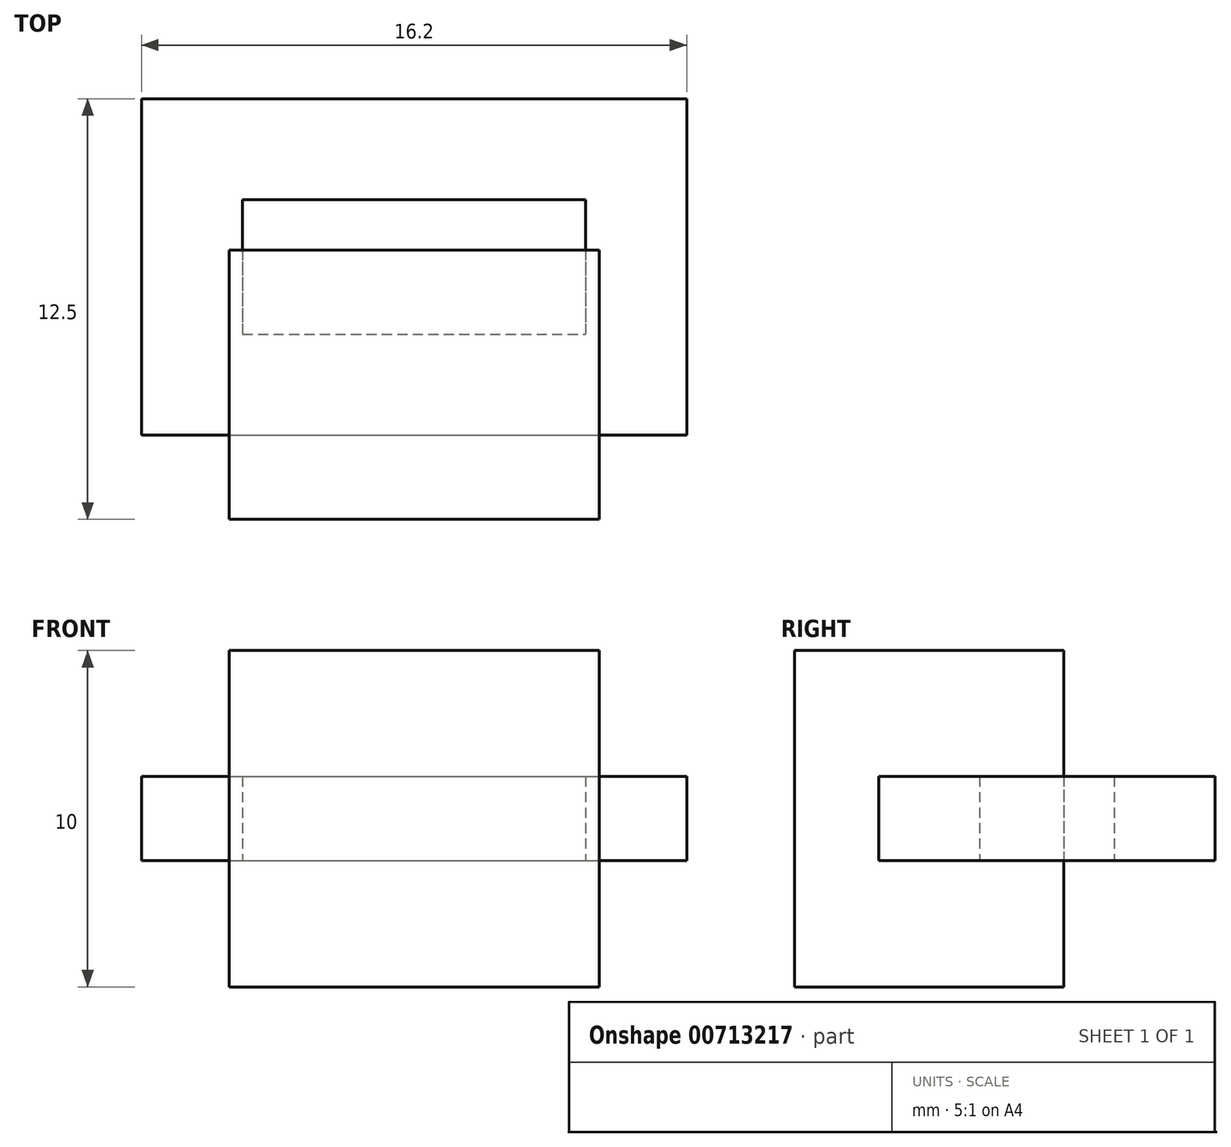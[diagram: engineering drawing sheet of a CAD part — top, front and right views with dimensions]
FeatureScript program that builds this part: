
annotation { "Feature Type Name" : "Feature", "Feature Type Description" : "" }
export const myFeature = defineFeature(function(context is Context, id is Id, definition is map)
    precondition{}
    {
        {
            var Q0;
            Q0=qCreatedBy(makeId("Top.planeOp"),FACE);
            var sketch = newSketch(context, id + "F0", { "sketchPlane" : qUnion([Q0])});
            skLineSegment(sketch, "E0.bottom", {"start": v(-8.1, -2) * mm, "end": v(8.1, -2) * mm});
            skLineSegment(sketch, "E0.top", {"start": v(-8.1, -12) * mm, "end": v(8.1, -12) * mm});
            skLineSegment(sketch, "E0.left", {"start": v(-8.1, -2) * mm, "end": v(-8.1, -12) * mm});
            skLineSegment(sketch, "E0.right", {"start": v(8.1, -2) * mm, "end": v(8.1, -12) * mm});
            skLineSegment(sketch, "E1.bottom", {"start": v(-5.1, -5) * mm, "end": v(5.1, -5) * mm});
            skLineSegment(sketch, "E1.top", {"start": v(-5.1, -9) * mm, "end": v(5.1, -9) * mm});
            skLineSegment(sketch, "E1.left", {"start": v(-5.1, -5) * mm, "end": v(-5.1, -9) * mm});
            skLineSegment(sketch, "E1.right", {"start": v(5.1, -5) * mm, "end": v(5.1, -9) * mm});
            skLineSegment(sketch, "E2", {"start": v(5.1, -9) * mm, "end": v(5.1, -12) * mm, "construction": true});
            skPoint(sketch, "E3", {"position": v(5.1, -10.5) * mm});
            skSolve(sketch);
        }
        {
            var Q0;
            Q0 = qSketchRegion(id + "F0", true);
            extrude(context, id + "F1", {"entities" : qUnion([Q0]), "endBound" : BoundingType.SYMMETRIC, "depth" : 2.5 * mm, "offsetDistance" : 25.4 * mm});
        }
        {
            var Q0;
            Q0=qCreatedBy(makeId("Top.planeOp"),FACE);
            var sketch = newSketch(context, id + "F2", { "sketchPlane" : qUnion([Q0])});
            skLineSegment(sketch, "E4.bottom", {"start": v(-5.5, -6.5) * mm, "end": v(5.5, -6.5) * mm});
            skLineSegment(sketch, "E4.top", {"start": v(-5.5, -14.5) * mm, "end": v(5.5, -14.5) * mm});
            skLineSegment(sketch, "E4.left", {"start": v(-5.5, -6.5) * mm, "end": v(-5.5, -14.5) * mm});
            skLineSegment(sketch, "E4.right", {"start": v(5.5, -6.5) * mm, "end": v(5.5, -14.5) * mm});
            skPoint(sketch, "E5.positionSnap0", {"position": v(0, -14.5) * mm});
            skPoint(sketch, "E6", {"position": v(5.5, -10.5) * mm});
            skSolve(sketch);
        }
        {
            var Q0;
            Q0 = qSketchRegion(id + "F2", true);
            extrude(context, id + "F3", {"entities" : qUnion([Q0]), "endBound" : BoundingType.SYMMETRIC, "depth" : 10 * mm, "offsetDistance" : 25.4 * mm});
        }
    });
